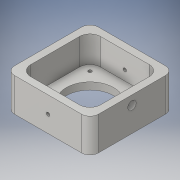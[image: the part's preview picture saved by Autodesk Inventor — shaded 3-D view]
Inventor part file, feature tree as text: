
AUTODESK INVENTOR PART (.ipt)
format: ipt  version: 2016 (Build 200138000, 138)  size: 330,752 bytes
history: native  units: in
note: dims shown in document units (in); Inventor stores cm internally (conversion verified against a paired STEP export)
features: sketch x6, extrude x4, fillet x2, projected_geometry x2, plane x1, hole x1, other x1
ambient origin geometry x8: Origin, YZ Plane, XZ Plane, XY Plane, X Axis, Y Axis, Z Axis, Center Point
bodies: Body1 (feature_tree)
feature tree (17):
  extrude  "Extrusion2"  Depth=2.5in
  fillet  "Fillet1"  Radius=1.0in
  extrude  "Extrusion3"  Depth=0.21in
  plane  "Work Plane1"
  fillet  "Fillet2"  Radius=0.79in
  sketch  "Sketch6"  dims[d29=90.0deg d30=0.3125in]
  hole  "Hole3"  [1 undecoded]
  sketch  "Sketch8"  dims[d31=0.1in d32=0.5in]
  extrude  "Extrusion6"  Depth=0.5in
  extrude  "Extrusion7"  Depth=1.0in TaperAngle=0.0deg
  sketch  "Sketch2"  dims[d3=2.5in d4=2.5in d5=1.0in d6=0.0in]
  sketch  "Sketch3"  dims[d7=0.25in d8=0.21in d9=0.79in d10=0.0in]
  projected_geometry  "Projected Loop1"
  other  "Work Axis1"
  projected_geometry  "Projected Loop4"
  sketch  "Sketch9"  dims[d33=1.0in]
  sketch  "Sketch10"  dims[d46=0.1in d47=0.75in d48=0.375in d49=0.25in d50=0.5635in d51=3.0in d52=0.8108in d53=0.1in d54=0.15in d55=0.15in d56=0.1in d57=0.15in d58=0.15in d59=1.0in d60=0.0in d61=0.25in d62=0.25in d63=0.0in]
note: 1 required parameter value undecoded (feature->parameter linkage not recoverable at this tier; creation-order binding heuristic only, values carry confidence <= 0.55)
